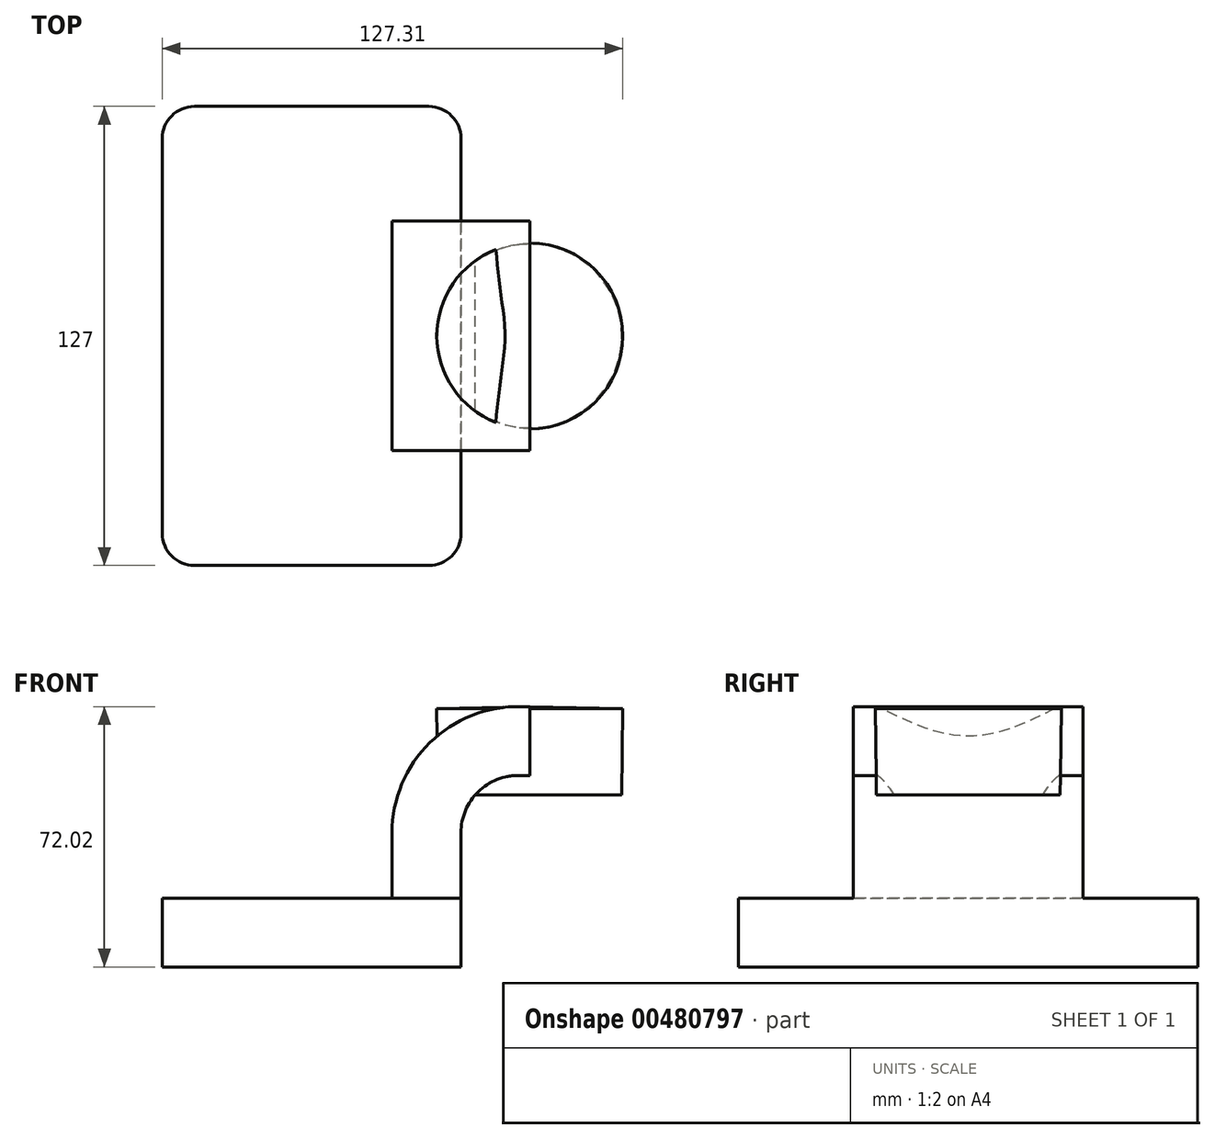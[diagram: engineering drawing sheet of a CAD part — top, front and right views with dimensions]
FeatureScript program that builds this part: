
annotation { "Feature Type Name" : "Feature", "Feature Type Description" : "" }
export const myFeature = defineFeature(function(context is Context, id is Id, definition is map)
    precondition{}
    {
        {
            var Q0;
            Q0=qCreatedBy(makeId("Front.planeOp"),FACE);
            var sketch = newSketch(context, id + "F0", { "sketchPlane" : qUnion([Q0])});
            skLineSegment(sketch, "E0.bottom", {"start": v(41.28, 9.52) * mm, "end": v(-41.28, 9.52) * mm});
            skLineSegment(sketch, "E0.top", {"start": v(41.28, -9.53) * mm, "end": v(-41.28, -9.53) * mm});
            skLineSegment(sketch, "E0.left", {"start": v(41.28, 9.52) * mm, "end": v(41.28, -9.53) * mm});
            skLineSegment(sketch, "E0.right", {"start": v(-41.28, 9.52) * mm, "end": v(-41.28, -9.53) * mm});
            skPoint(sketch, "E0.middle", {"position": v(0, 0) * mm});
            skLineSegment(sketch, "E1.bottom", {"start": v(111.12, 66.67) * mm, "end": v(60.33, 66.67) * mm});
            skLineSegment(sketch, "E1.top", {"start": v(111.12, 38.1) * mm, "end": v(60.33, 38.1) * mm});
            skLineSegment(sketch, "E1.left", {"start": v(111.12, 66.67) * mm, "end": v(111.12, 38.1) * mm});
            skLineSegment(sketch, "E1.right", {"start": v(60.33, 66.67) * mm, "end": v(60.33, 38.1) * mm});
            skPoint(sketch, "E1.middle", {"position": v(85.72, 52.39) * mm});
            skLineSegment(sketch, "E2", {"start": v(41.28, 9.52) * mm, "end": v(41.28, 27.56) * mm});
            skArc(sketch, "E3", {"start": v(41.27, 27.56) * mm, "mid": v(46.04, 38.9) * mm, "end": v(57.46, 43.43) * mm});
            skLineSegment(sketch, "E4", {"start": v(57.46, 43.43) * mm, "end": v(85.72, 42.88) * mm});
            skLineSegment(sketch, "E5.0", {"start": v(57.84, 62.48) * mm, "end": v(86.1, 61.92) * mm});
            skArc(sketch, "E5.1", {"start": v(22.23, 27.56) * mm, "mid": v(32.7, 52.5) * mm, "end": v(57.84, 62.48) * mm});
            skLineSegment(sketch, "E5.2", {"start": v(22.22, 9.52) * mm, "end": v(22.22, 27.56) * mm});
            skLineSegment(sketch, "E6", {"start": v(85.72, 38.1) * mm, "end": v(86.1, 66.67) * mm});
            skFitSpline(sketch, "E7", {"points": [v(-41.28, 9.52) * mm, v(57.84, 62.48) * mm], "startDerivative": vector(0.46, 102.5) * mm, "endDerivative": vector(191.52, -9.6) * mm});
            skSolve(sketch);
        }
        {
            var Q0;
            Q0=makeQuery(id+"F0.imprint","IMPRINT",FACE,{"disambiguationData":[TD([[makeQuery(id+"F0.imprint","IMPRINT",EDGE,{"derivedFrom":sQuery(id+"F0.wireOp",EDGE,"E0.top")}),-1.0]])]});
            extrude(context, id + "F1", {"entities" : qUnion([Q0]), "endBound" : BoundingType.SYMMETRIC, "oppositeDirection" : true, "depth" : 127 * mm});
        }
        {
            var Q0;
            {var subQ1=sQuery(id+"F0.wireOp",EDGE,"E2");Q0=makeQuery(id+"F0.imprint","IMPRINT",FACE,{"disambiguationData":[TD([[makeQuery(id+"F0.imprint","IMPRINT",EDGE,{"derivedFrom":subQ1}),1.0]])]});}
            extrude(context, id + "F2", {"entities" : qUnion([Q0]), "operationType" : NewBodyOperationType.ADD, "endBound" : BoundingType.SYMMETRIC, "depth" : 63.5 * mm});
        }
        {
            var Q0;
            Q0=makeQuery(id+"F0.imprint","IMPRINT",FACE,{"disambiguationData":[TD([[makeQuery(id+"F0.imprint","IMPRINT",EDGE,{"derivedFrom":sQuery(id+"F0.wireOp",EDGE,"E5.1")}),1.0]])]});
            extrude(context, id + "F3", {"entities" : qUnion([Q0]), "operationType" : NewBodyOperationType.ADD, "depth" : 15.88 * mm});
        }
        {
            var Q0;
            {var subQ1=sQuery(id+"F0.wireOp",EDGE,"E1.right");var subQ5=sQuery(id+"F0.wireOp",EDGE,"E1.top");var subQ6=makeQuery(id+"F0.imprint","INTERSECT",VERTEX,{"derivedFrom":[subQ5,subQ1]});Q0=makeQuery(id+"F0.imprint","IMPRINT",FACE,{"disambiguationData":[TD([[makeQuery(id+"F0.imprint","IMPRINT",EDGE,{"disambiguationData":[TD([[subQ6,1.0]])],"derivedFrom":subQ5}),-1.0]])]});}
            var Q1;
            Q1=sQuery(id+"F0.wireOp",EDGE,"E1.right");
            revolve(context, id + "F4", {"operationType" : NewBodyOperationType.ADD, "entities" : qUnion([Q0]), "axis" : qUnion([Q1]), "revolveType" : RevolveType.FULL});
        }
        {
            var Q0;
            Q0=makeQuery(id+"F1.opExtrude","CAP_EDGE",EDGE,{"disambiguationData":[OSD([sQuery(id+"F0.wireOp",EDGE,"E0.left")])],"isStart":false});
            var Q1;
            Q1=makeQuery(id+"F1.opExtrude","CAP_EDGE",EDGE,{"disambiguationData":[OSD([sQuery(id+"F0.wireOp",EDGE,"E0.left")])],"isStart":true});
            var Q2;
            Q2=makeQuery(id+"F1.opExtrude","CAP_EDGE",EDGE,{"disambiguationData":[OSD([sQuery(id+"F0.wireOp",EDGE,"E0.right")])],"isStart":true});
            var Q3;
            Q3=makeQuery(id+"F1.opExtrude","CAP_EDGE",EDGE,{"disambiguationData":[OSD([sQuery(id+"F0.wireOp",EDGE,"E0.right")])],"isStart":false});
            fillet(context, id + "F5", {"entities" : qUnion([Q0, Q1, Q2, Q3]), "radius" : 8.9 * mm, "tangentPropagation" : true, "allowEdgeOverflow" : false});
        }
    });
